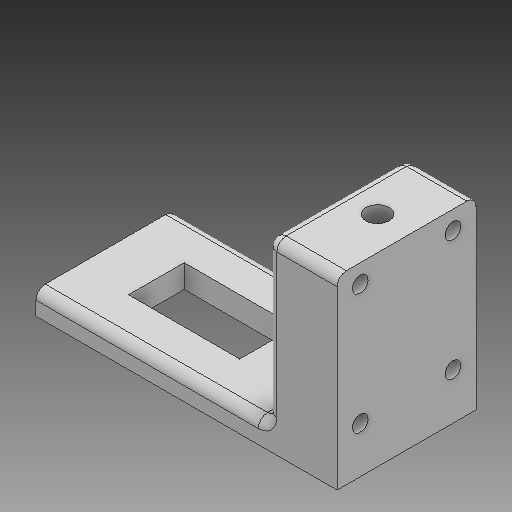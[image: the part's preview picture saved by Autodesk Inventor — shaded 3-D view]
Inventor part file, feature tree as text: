
AUTODESK INVENTOR PART (.ipt)
format: ipt  version: 2018 (Build 220112000, 112)  size: 138,752 bytes
history: native  units: mm
features: sketch x5, other x3
ambient origin geometry x8: Origin, YZ Plane, XZ Plane, XY Plane, X Axis, Y Axis, Z Axis, Center Point
bodies: Volumenkörper1 (feature_tree)
feature tree (8):
  other  "L-Halterung Servo.ipt"
  other  "Volumenkörper1::L-Halterung Servo.ipt"
  other  "Bezeichnung1"
  sketch  "Skizze1"  dims[d0=10.0mm]
  sketch  "Skizze2"
  sketch  "Skizze3"
  sketch  "Skizze4"
  sketch  "Skizze5"
